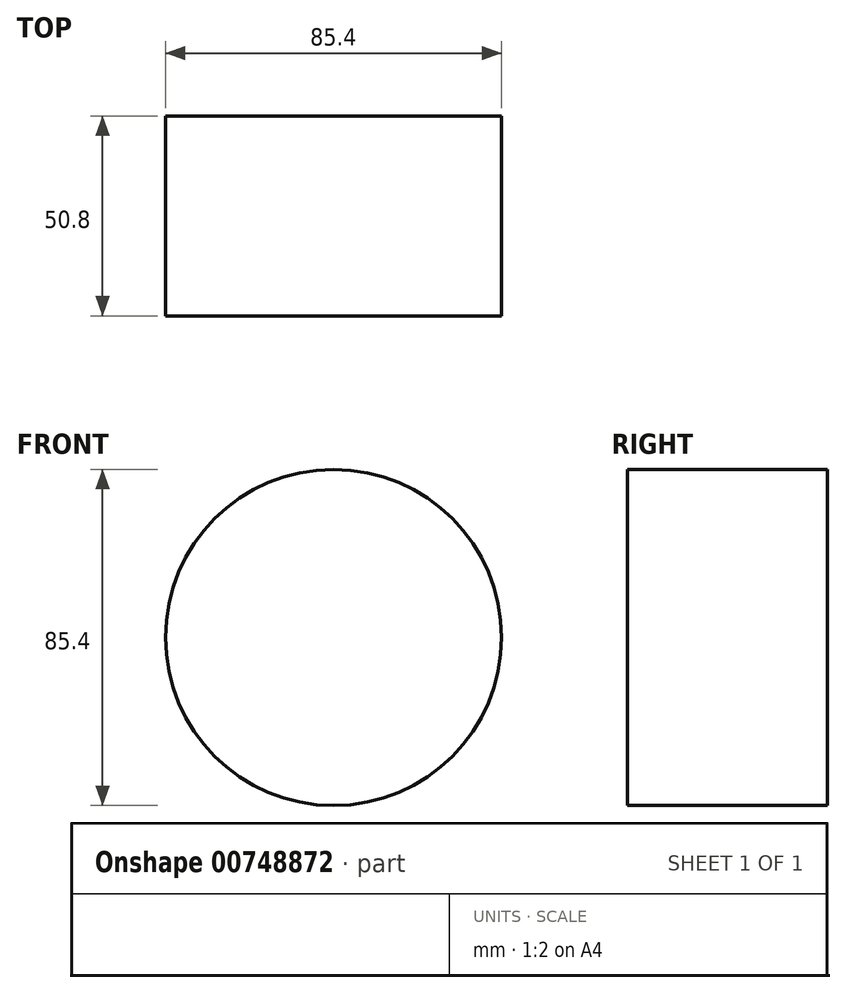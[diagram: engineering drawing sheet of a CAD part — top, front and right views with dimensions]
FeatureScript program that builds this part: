
annotation { "Feature Type Name" : "Feature", "Feature Type Description" : "" }
export const myFeature = defineFeature(function(context is Context, id is Id, definition is map)
    precondition{}
    {
        {
            var Q0;
            Q0=qCreatedBy(makeId("Front.planeOp"),FACE);
            var sketch = newSketch(context, id + "F0", { "sketchPlane" : qUnion([Q0])});
            skCircle(sketch, "E0", {"center": v(0, 0) * mm, "radius": 42.7 * mm});
            skSolve(sketch);
        }
        {
            var Q0;
            Q0=makeQuery(id+"F0.imprint","IMPRINT",FACE,{"disambiguationData":[TD([[makeQuery(id+"F0.imprint","IMPRINT",EDGE,{"derivedFrom":sQuery(id+"F0.wireOp",EDGE,"E0")}),1.0]])]});
            extrude(context, id + "F1", {"entities" : qUnion([Q0]), "depth" : 50.8 * mm, "offsetDistance" : 25.4 * mm});
        }
    });
